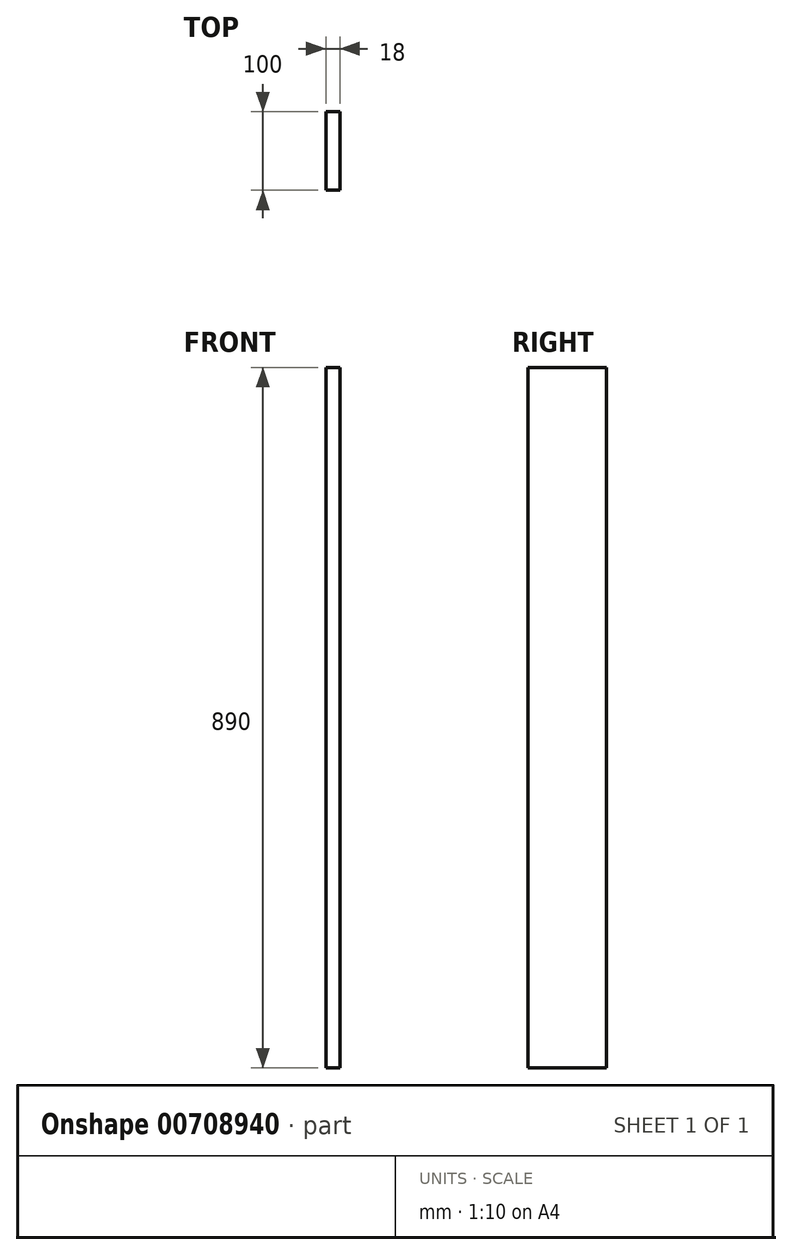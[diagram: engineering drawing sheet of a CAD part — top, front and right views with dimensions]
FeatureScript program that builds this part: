
annotation { "Feature Type Name" : "Feature", "Feature Type Description" : "" }
export const myFeature = defineFeature(function(context is Context, id is Id, definition is map)
    precondition{}
    {
        {
            var Q0;
            Q0=qCreatedBy(makeId("Top.planeOp"),FACE);
            var sketch = newSketch(context, id + "F0", { "sketchPlane" : qUnion([Q0])});
            skLineSegment(sketch, "E0.bottom", {"start": v(0, 0) * mm, "end": v(18, 0) * mm});
            skLineSegment(sketch, "E0.top", {"start": v(0, 100) * mm, "end": v(18, 100) * mm});
            skLineSegment(sketch, "E0.left", {"start": v(0, 0) * mm, "end": v(0, 100) * mm});
            skLineSegment(sketch, "E0.right", {"start": v(18, 0) * mm, "end": v(18, 100) * mm});
            skSolve(sketch);
        }
        {
            var Q0;
            Q0=makeQuery(id+"F0.imprint","IMPRINT",FACE,{"disambiguationData":[TD([[makeQuery(id+"F0.imprint","IMPRINT",EDGE,{"derivedFrom":sQuery(id+"F0.wireOp",EDGE,"E0.bottom")}),1.0]])]});
            extrude(context, id + "F1", {"entities" : qUnion([Q0]), "depth" : 890 * mm, "offsetDistance" : 25 * mm});
        }
    });
